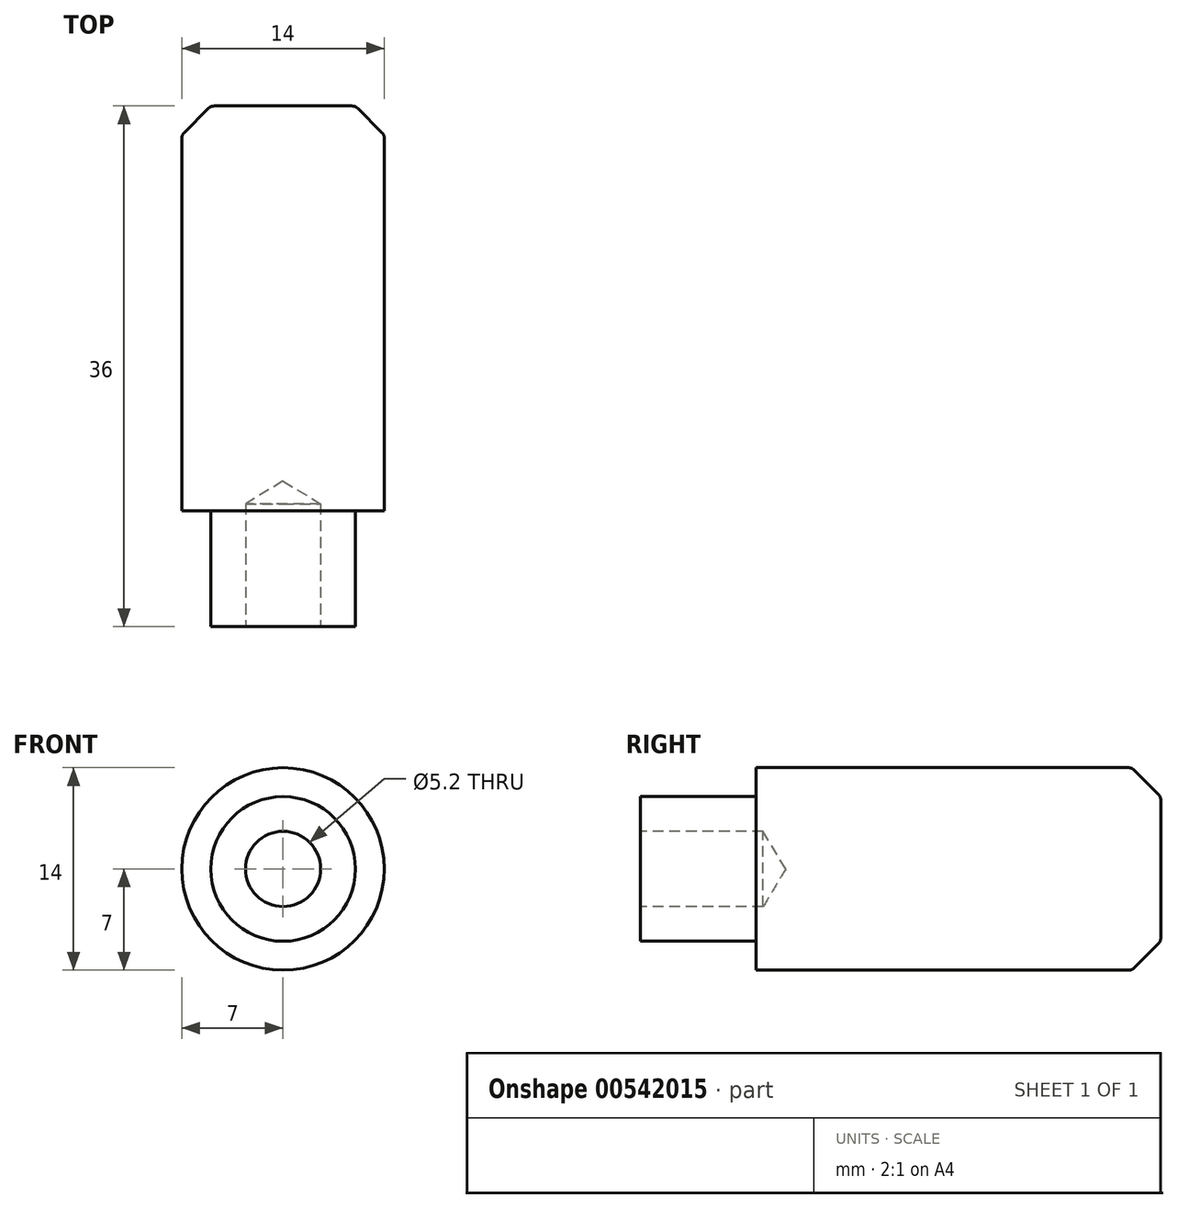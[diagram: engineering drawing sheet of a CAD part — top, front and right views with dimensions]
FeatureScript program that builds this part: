
annotation { "Feature Type Name" : "Feature", "Feature Type Description" : "" }
export const myFeature = defineFeature(function(context is Context, id is Id, definition is map)
    precondition{}
    {
        {
            var Q0;
            Q0=qCreatedBy(makeId("Right.planeOp"),FACE);
            var sketch = newSketch(context, id + "F0", { "sketchPlane" : qUnion([Q0])});
            skLineSegment(sketch, "E0.bottom", {"start": v(-36, 0) * mm, "end": v(0, 0) * mm});
            skLineSegment(sketch, "E0.top", {"start": v(-28, 7) * mm, "end": v(-2.2, 7) * mm});
            skLineSegment(sketch, "E0.left", {"start": v(-36, 0) * mm, "end": v(-36, 5) * mm});
            skLineSegment(sketch, "E0.right", {"start": v(0, 0) * mm, "end": v(0, 4.8) * mm});
            skLineSegment(sketch, "E1", {"start": v(-36, 5) * mm, "end": v(-28, 5) * mm});
            skLineSegment(sketch, "E2", {"start": v(-28, 5) * mm, "end": v(-28, 7) * mm});
            skLineSegment(sketch, "E3", {"start": v(-1.85, 6.85) * mm, "end": v(-0.15, 5.15) * mm});
            skPoint(sketch, "E4.visualSharp", {"position": v(-2, 7) * mm});
            skArc(sketch, "E4.filletArc", {"start": v(-1.85, 6.85) * mm, "mid": v(-2.02, 6.96) * mm, "end": v(-2.2, 7) * mm});
            skPoint(sketch, "E5.visualSharp", {"position": v(0, 5) * mm});
            skArc(sketch, "E5.filletArc", {"start": v(0, 4.8) * mm, "mid": v(-0.04, 4.98) * mm, "end": v(-0.15, 5.15) * mm});
            skSolve(sketch);
        }
        {
            var Q0;
            Q0 = qSketchRegion(id + "F0", true);
            var Q1;
            Q1=sQuery(id+"F0.wireOp",EDGE,"E0.bottom");
            revolve(context, id + "F1", {"entities" : qUnion([Q0]), "axis" : qUnion([Q1]), "revolveType" : RevolveType.FULL});
        }
        {
            var Q0;
            Q0=makeQuery(id+"F1.opRevolve","SWEPT_FACE",FACE,{"disambiguationData":[OSD([sQuery(id+"F0.wireOp",EDGE,"E0.left")])]});
            var sketch = newSketch(context, id + "F2", { "sketchPlane" : qUnion([Q0])});
            skLineSegment(sketch, "E6", {"start": v(-2, 0) * mm, "end": v(2, 0) * mm, "construction": true});
            skLineSegment(sketch, "E7", {"start": v(0, 2) * mm, "end": v(0, -2) * mm, "construction": true});
            skPoint(sketch, "E8.start.orphan", {"position": v(0, 0) * mm});
            skSolve(sketch);
        }
        {
            var Q0;
            Q0=sQuery(id+"F2.wireOp",VERTEX,"E8.start.orphan");
            var Q1;
            Q1=makeQuery(id+"F1.opRevolve","SWEPT_BODY",BODY,{"disambiguationData":[OSD([sQuery(id+"F0.wireOp",EDGE,"E0.bottom"),sQuery(id+"F0.wireOp",EDGE,"E0.top"),sQuery(id+"F0.wireOp",EDGE,"E0.left"),sQuery(id+"F0.wireOp",EDGE,"E0.right"),sQuery(id+"F0.wireOp",EDGE,"E1"),sQuery(id+"F0.wireOp",EDGE,"E2"),sQuery(id+"F0.wireOp",EDGE,"E3"),sQuery(id+"F0.wireOp",EDGE,"E4.filletArc"),sQuery(id+"F0.wireOp",EDGE,"E5.filletArc")])]});
            hole(context, id + "F3", {"style" : HoleStyle.SIMPLE, "endStyle" : HoleEndStyle.BLIND, "standardTappedOrClearance" : lookupTablePath({ "standard" : "ISO", "size" : "5.2", "type" : "Drilled" }), "standardBlindInLast" : lookupTablePath({ "standard" : "ISO", "size" : "5.2", "type" : "Drilled" }), "holeDiameter" : 5.2 * mm, "holeDepth" : 8.5 * mm, "isTappedThrough" : true, "tappedDepth" : 4.2 * mm, "tapClearance" : 3, "locations" : qUnion([Q0]), "scope" : qUnion([Q1])});
        }
    });
